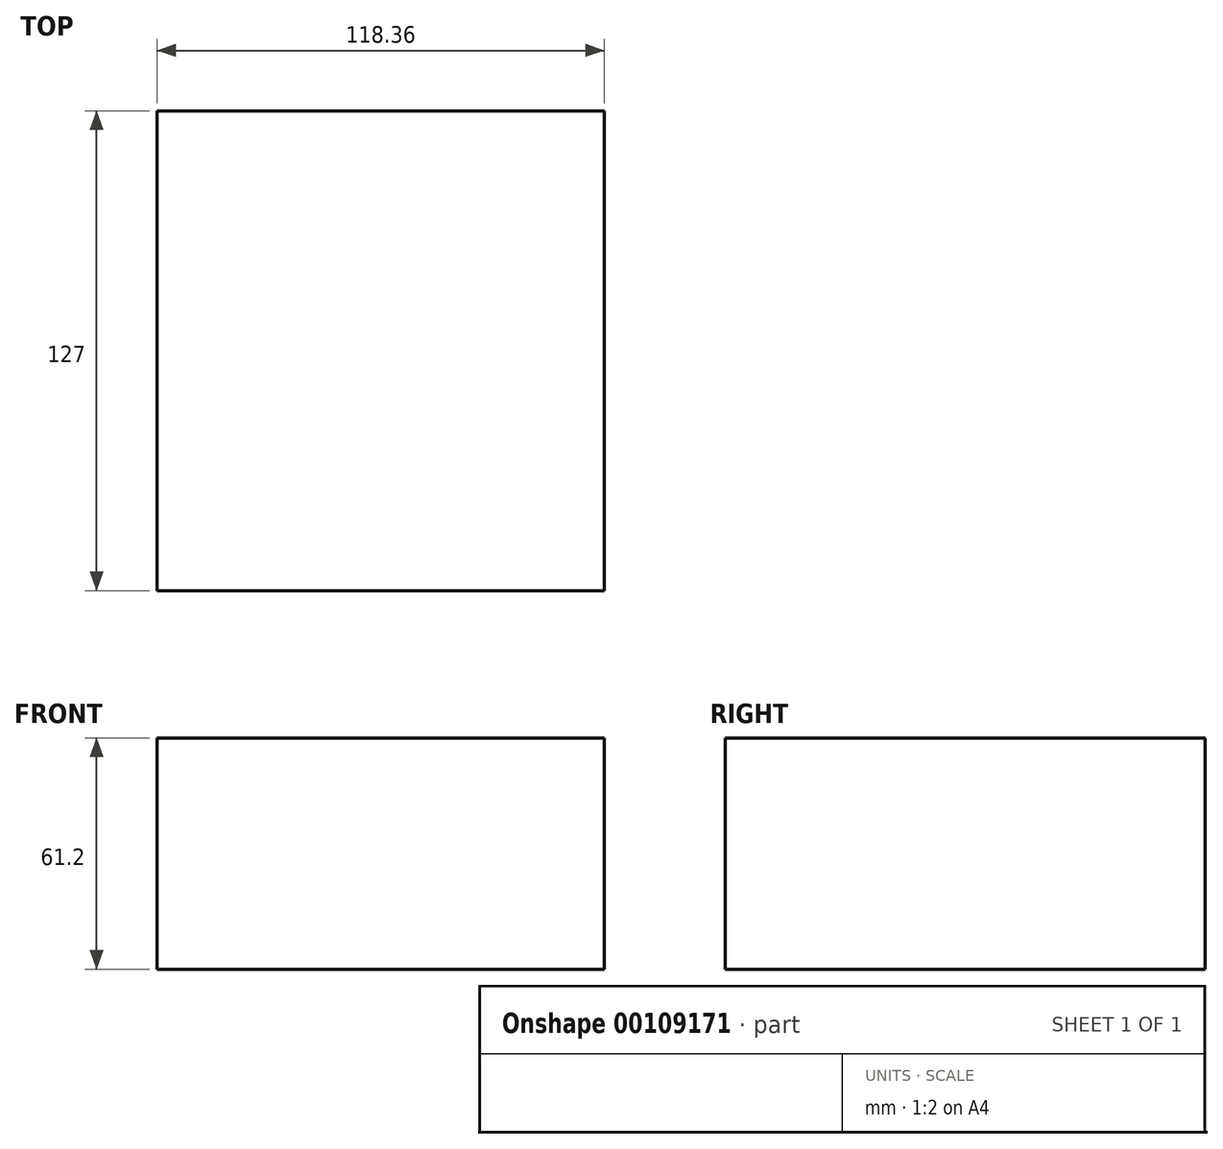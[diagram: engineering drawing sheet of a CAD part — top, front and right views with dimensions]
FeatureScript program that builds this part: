
annotation { "Feature Type Name" : "Feature", "Feature Type Description" : "" }
export const myFeature = defineFeature(function(context is Context, id is Id, definition is map)
    precondition{}
    {
        {
            var Q0;
            Q0=qCreatedBy(makeId("Front.planeOp"),FACE);
            var sketch = newSketch(context, id + "F0", { "sketchPlane" : qUnion([Q0])});
            skLineSegment(sketch, "E0.bottom", {"start": v(59.18, -30.6) * mm, "end": v(-59.18, -30.6) * mm});
            skLineSegment(sketch, "E0.top", {"start": v(59.18, 30.6) * mm, "end": v(-59.18, 30.6) * mm});
            skLineSegment(sketch, "E0.left", {"start": v(59.18, -30.6) * mm, "end": v(59.18, 30.6) * mm});
            skLineSegment(sketch, "E0.right", {"start": v(-59.18, -30.6) * mm, "end": v(-59.18, 30.6) * mm});
            skPoint(sketch, "E0.middle", {"position": v(0, 0) * mm});
            skSolve(sketch);
        }
        {
            var Q0;
            Q0=makeQuery(id+"F0.imprint","IMPRINT",FACE,{"disambiguationData":[TD([[makeQuery(id+"F0.imprint","IMPRINT",EDGE,{"derivedFrom":sQuery(id+"F0.wireOp",EDGE,"E0.bottom")}),-1.0]])]});
            extrude(context, id + "F1", {"entities" : qUnion([Q0]), "depth" : 127 * mm});
        }
    });
